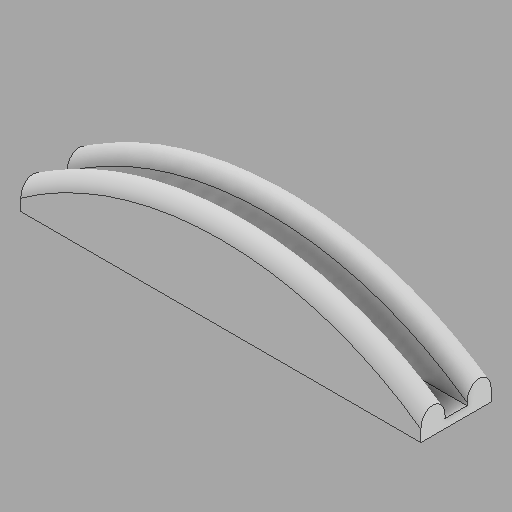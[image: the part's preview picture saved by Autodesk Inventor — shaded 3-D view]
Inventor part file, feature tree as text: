
AUTODESK INVENTOR PART (.ipt)
format: ipt  version: 2025.2 (Build 292293000, 293)  size: 208,896 bytes
history: native  units: in
note: dims shown in document units (in); Inventor stores cm internally (conversion verified against a paired STEP export)
features: sketch x5, extrude x3, hole x2, chamfer x1, fillet x1
ambient origin geometry x8: Origin, YZ Plane, XZ Plane, XY Plane, X Axis, Y Axis, Z Axis, Center Point
bodies: Solid1 (feature_tree)
feature tree (12):
  extrude  "Extrusion1"  Depth=5.6875in
  extrude  "Extrusion2"  Depth=1.0in TaperAngle=0.0deg
  extrude  "Extrusion3"  Depth=0.3125in
  hole  "Hole1"  [1 undecoded]
  hole  "Hole2"  [1 undecoded]
  chamfer  "Chamfer2"  Distance=0.625in
  fillet  "Fillet2"  Radius=0.5625in
  sketch  "Sketch1"  dims[d0=0.375in d1=5.6875in]
  sketch  "Sketch2"  dims[d2=1.25in d3=1.0in d4=0.0in]
  sketch  "Sketch3"  dims[d5=0.125in d6=0.3125in]
  sketch  "Sketch4"  dims[d7=0.0in d8=0.0in d9=0.3125in]
  sketch  "Sketch5"  dims[d10=1.0in d11=0.0in d12=0.0in d13=0.625in d14=0.5625in d16=0.2188in d18=0.2188in d19=0.1875in d20=0.75in d21=0.375in d22=0.25in d23=0.5635in d24=0.375in d25=0.0in d30=3.0in d31=0.1875in d32=0.75in d33=0.375in d34=0.25in d35=0.5635in d36=0.25in d37=0.0in d38=0.0312in d39=0.125in d40=45.0deg d41=0.1719in]
note: 2 required parameter values undecoded (feature->parameter linkage not recoverable at this tier; creation-order binding heuristic only, values carry confidence <= 0.55)
